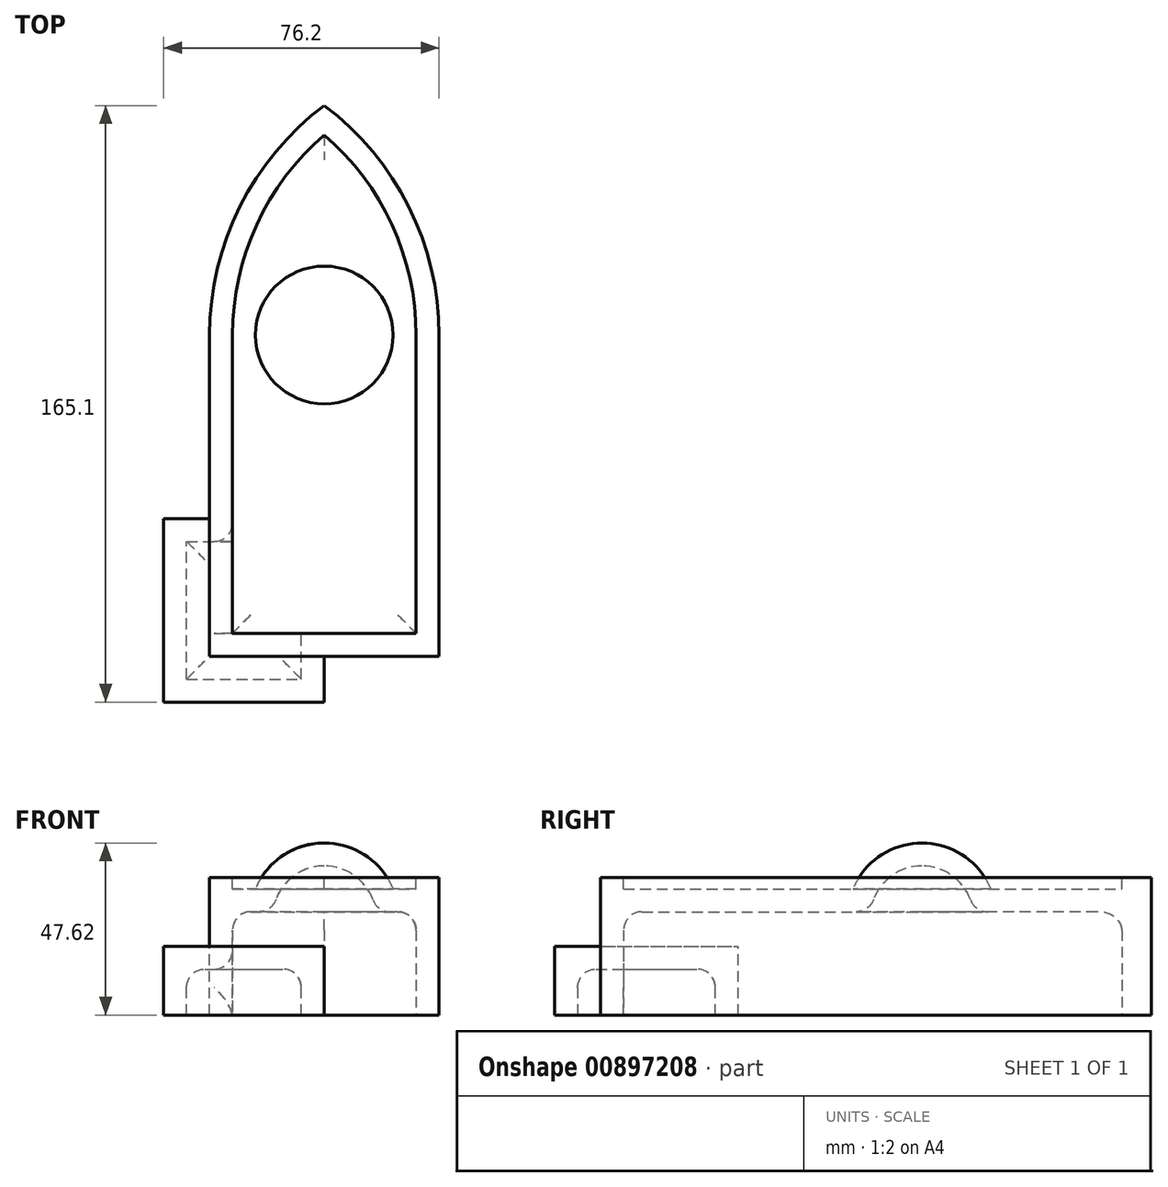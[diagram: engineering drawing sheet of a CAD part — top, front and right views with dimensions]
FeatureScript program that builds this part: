
annotation { "Feature Type Name" : "Feature", "Feature Type Description" : "" }
export const myFeature = defineFeature(function(context is Context, id is Id, definition is map)
    precondition{}
    {
        {
            var Q0;
            Q0=qCreatedBy(makeId("Top.planeOp"),FACE);
            var sketch = newSketch(context, id + "F0", { "sketchPlane" : qUnion([Q0])});
            skLineSegment(sketch, "E0.bottom", {"start": v(0, 0) * mm, "end": v(63.5, 0) * mm});
            skLineSegment(sketch, "E0.top", {"start": v(0, 88.9) * mm, "end": v(63.5, 88.9) * mm, "construction": true});
            skLineSegment(sketch, "E0.left", {"start": v(0, 0) * mm, "end": v(0, 88.9) * mm});
            skLineSegment(sketch, "E0.right", {"start": v(63.5, 0) * mm, "end": v(63.5, 88.9) * mm});
            skLineSegment(sketch, "E1", {"start": v(31.75, 0) * mm, "end": v(31.75, 152.4) * mm, "construction": true});
            skArc(sketch, "E2", {"start": v(31.75, 152.4) * mm, "mid": v(8.38, 124.4) * mm, "end": v(0, 88.9) * mm});
            skArc(sketch, "E3.MirrorCS", {"start": v(31.75, 152.4) * mm, "mid": v(55.12, 124.4) * mm, "end": v(63.5, 88.9) * mm});
            skSolve(sketch);
        }
        {
            var Q0;
            Q0 = qSketchRegion(id + "F0", true);
            extrude(context, id + "F1", {"entities" : qUnion([Q0]), "depth" : 38.1 * mm, "offsetDistance" : 25.4 * mm});
        }
        {
            var Q0;
            Q0=makeQuery(id+"F1.opExtrude","SWEPT_FACE",FACE,{"disambiguationData":[OSD([sQuery(id+"F0.wireOp",EDGE,"E0.left")])]});
            var sketch = newSketch(context, id + "F2", { "sketchPlane" : qUnion([Q0])});
            skLineSegment(sketch, "E4.bottom", {"start": v(0, 0) * mm, "end": v(-38.1, 0) * mm});
            skLineSegment(sketch, "E4.top", {"start": v(0, 19.05) * mm, "end": v(-38.1, 19.05) * mm});
            skLineSegment(sketch, "E4.left", {"start": v(0, 0) * mm, "end": v(0, 19.05) * mm});
            skLineSegment(sketch, "E4.right", {"start": v(-38.1, 0) * mm, "end": v(-38.1, 19.05) * mm});
            skSolve(sketch);
        }
        {
            var Q0;
            Q0 = qSketchRegion(id + "F2", true);
            extrude(context, id + "F3", {"entities" : qUnion([Q0]), "operationType" : NewBodyOperationType.ADD, "depth" : 12.7 * mm, "offsetDistance" : 25.4 * mm});
        }
        {
            var Q0;
            Q0=makeQuery(id+"F3.boolean.opBoolean","MERGE",FACE,{"derivedFrom":[makeQuery(id+"F1.opExtrude","SWEPT_FACE",FACE,{"disambiguationData":[OSD([sQuery(id+"F0.wireOp",EDGE,"E0.bottom")])]}),makeQuery(id+"F3.opExtrude","SWEPT_FACE",FACE,{"disambiguationData":[OSD([sQuery(id+"F2.wireOp",EDGE,"E4.left")])]})]});
            var sketch = newSketch(context, id + "F4", { "sketchPlane" : qUnion([Q0])});
            skLineSegment(sketch, "E5.bottom", {"start": v(-12.7, 0) * mm, "end": v(31.75, 0) * mm});
            skLineSegment(sketch, "E5.top", {"start": v(-12.7, 19.05) * mm, "end": v(31.75, 19.05) * mm});
            skLineSegment(sketch, "E5.left", {"start": v(-12.7, 0) * mm, "end": v(-12.7, 19.05) * mm});
            skLineSegment(sketch, "E5.right", {"start": v(31.75, 0) * mm, "end": v(31.75, 19.05) * mm});
            skSolve(sketch);
        }
        {
            var Q0;
            Q0 = qSketchRegion(id + "F4", true);
            extrude(context, id + "F5", {"entities" : qUnion([Q0]), "operationType" : NewBodyOperationType.ADD, "depth" : 12.7 * mm, "offsetDistance" : 25.4 * mm});
        }
        {
            var Q0;
            Q0=makeQuery(id+"F1.opExtrude","CAP_FACE",FACE,{"disambiguationData":[OSD([sQuery(id+"F0.wireOp",EDGE,"E0.bottom"),sQuery(id+"F0.wireOp",EDGE,"E0.left"),sQuery(id+"F0.wireOp",EDGE,"E0.right"),sQuery(id+"F0.wireOp",EDGE,"E2"),sQuery(id+"F0.wireOp",EDGE,"E3.MirrorCS")])],"isStart":false});
            var sketch = newSketch(context, id + "F6", { "sketchPlane" : qUnion([Q0])});
            skLineSegment(sketch, "E6.0", {"start": v(6.35, 6.35) * mm, "end": v(6.35, 88.9) * mm});
            skArc(sketch, "E6.1", {"start": v(31.75, 144.26) * mm, "mid": v(13, 119.35) * mm, "end": v(6.35, 88.9) * mm});
            skLineSegment(sketch, "E6.2", {"start": v(6.35, 6.35) * mm, "end": v(57.15, 6.35) * mm});
            skLineSegment(sketch, "E6.3", {"start": v(57.15, 6.35) * mm, "end": v(57.15, 88.9) * mm});
            skArc(sketch, "E6.4", {"start": v(31.75, 144.26) * mm, "mid": v(50.5, 119.35) * mm, "end": v(57.15, 88.9) * mm});
            skSolve(sketch);
        }
        {
            var Q0;
            Q0 = qSketchRegion(id + "F6", true);
            extrude(context, id + "F7", {"entities" : qUnion([Q0]), "operationType" : NewBodyOperationType.REMOVE, "oppositeDirection" : true, "depth" : 3.17 * mm, "offsetDistance" : 25.4 * mm});
        }
        {
            var Q0;
            Q0=makeQuery(id+"F1.opExtrude","SWEPT_EDGE",EDGE,{"disambiguationData":[OSD([sQuery(id+"F0.wireOp",EDGE,"E0.left"),sQuery(id+"F0.wireOp",EDGE,"E2")])]});
            cPoint(context, id + "F8", {"entities" : qUnion([Q0]), "parameter" : 0.5});
        }
        {
            var Q0;
            Q0=qCreatedBy(makeId("Front.planeOp"),FACE);
            var Q1;
            Q1 = qCreatedBy(id + "F8" ,VERTEX);
            cPlane(context, id + "F9", {"entities" : qUnion([Q0, Q1]), "cplaneType" : CPlaneType.PLANE_POINT, "offset" : 0 * mm, "width" : 152.4 * mm, "height" : 152.4 * mm});
        }
        {
            var Q0;
            Q0=qCreatedBy(id+"F9.planeOp",FACE);
            var sketch = newSketch(context, id + "F10", { "sketchPlane" : qUnion([Q0])});
            skLineSegment(sketch, "E7.0", {"start": v(0, 38.1) * mm, "end": v(63.5, 38.1) * mm, "construction": true});
            skLineSegment(sketch, "E8", {"start": v(31.75, 38.1) * mm, "end": v(31.75, 80.25) * mm, "construction": true});
            skLineSegment(sketch, "E9", {"start": v(6.64, 34.93) * mm, "end": v(55.04, 34.93) * mm, "construction": true});
            skArc(sketch, "E10", {"start": v(31.75, 47.63) * mm, "mid": v(20.3, 44.16) * mm, "end": v(12.7, 34.92) * mm});
            skLineSegment(sketch, "E11", {"start": v(31.75, 47.63) * mm, "end": v(31.75, 34.93) * mm});
            skPoint(sketch, "E11.endSnap0", {"position": v(30.84, 34.93) * mm});
            skLineSegment(sketch, "E12", {"start": v(31.75, 34.93) * mm, "end": v(12.7, 34.92) * mm});
            skSolve(sketch);
        }
        {
            var Q0;
            Q0 = qSketchRegion(id + "F10", true);
            var Q1;
            Q1=sQuery(id+"F10.wireOp",EDGE,"E8");
            revolve(context, id + "F11", {"operationType" : NewBodyOperationType.ADD, "surfaceOperationType" : NewSurfaceOperationType.NEW, "entities" : qUnion([Q0]), "axis" : qUnion([Q1]), "revolveType" : RevolveType.FULL});
        }
        {
            var Q0;
            Q0=makeQuery(id+"F5.boolean.opBoolean","MERGE",FACE,{"derivedFrom":[makeQuery(id+"F3.boolean.opBoolean","MERGE",FACE,{"derivedFrom":[makeQuery(id+"F1.opExtrude","CAP_FACE",FACE,{"disambiguationData":[OSD([sQuery(id+"F0.wireOp",EDGE,"E0.bottom"),sQuery(id+"F0.wireOp",EDGE,"E0.left"),sQuery(id+"F0.wireOp",EDGE,"E0.right"),sQuery(id+"F0.wireOp",EDGE,"E2"),sQuery(id+"F0.wireOp",EDGE,"E3.MirrorCS")])],"isStart":true}),makeQuery(id+"F3.opExtrude","SWEPT_FACE",FACE,{"disambiguationData":[OSD([sQuery(id+"F2.wireOp",EDGE,"E4.bottom")])]})]}),makeQuery(id+"F5.opExtrude","SWEPT_FACE",FACE,{"disambiguationData":[OSD([sQuery(id+"F4.wireOp",EDGE,"E5.bottom")])]})]});
            shell(context, id + "F12", {"entities" : qUnion([Q0]), "thickness" : 6.35 * mm});
        }
        {
            var Q0;
            Q0=makeQuery(id+"F12.opShell","TWEAK_EDGE",EDGE,{"derivedFrom":[makeQuery(id+"F1.opExtrude","SWEPT_FACE",FACE,{"disambiguationData":[OSD([sQuery(id+"F0.wireOp",EDGE,"E0.left")])]}),makeQuery(id+"F7.boolean.opBoolean","COPY",FACE,{"derivedFrom":makeQuery(id+"F7.opExtrude","CAP_FACE",FACE,{"disambiguationData":[OSD([sQuery(id+"F6.wireOp",EDGE,"E6.0"),sQuery(id+"F6.wireOp",EDGE,"E6.1"),sQuery(id+"F6.wireOp",EDGE,"E6.2"),sQuery(id+"F6.wireOp",EDGE,"E6.3"),sQuery(id+"F6.wireOp",EDGE,"E6.4")])],"isStart":false})})]});
            var Q1;
            Q1=makeQuery(id+"F12.opShell","TWEAK_EDGE",EDGE,{"derivedFrom":[makeQuery(id+"F1.opExtrude","SWEPT_FACE",FACE,{"disambiguationData":[OSD([sQuery(id+"F0.wireOp",EDGE,"E3.MirrorCS")])]}),makeQuery(id+"F7.boolean.opBoolean","COPY",FACE,{"derivedFrom":makeQuery(id+"F7.opExtrude","CAP_FACE",FACE,{"disambiguationData":[OSD([sQuery(id+"F6.wireOp",EDGE,"E6.0"),sQuery(id+"F6.wireOp",EDGE,"E6.1"),sQuery(id+"F6.wireOp",EDGE,"E6.2"),sQuery(id+"F6.wireOp",EDGE,"E6.3"),sQuery(id+"F6.wireOp",EDGE,"E6.4")])],"isStart":false})})]});
            var Q2;
            Q2=makeQuery(id+"F12.opShell","TWEAK_EDGE",EDGE,{"derivedFrom":[makeQuery(id+"F3.boolean.opBoolean","MERGE",FACE,{"derivedFrom":[makeQuery(id+"F1.opExtrude","SWEPT_FACE",FACE,{"disambiguationData":[OSD([sQuery(id+"F0.wireOp",EDGE,"E0.bottom")])]}),makeQuery(id+"F3.opExtrude","SWEPT_FACE",FACE,{"disambiguationData":[OSD([sQuery(id+"F2.wireOp",EDGE,"E4.left")])]})]}),makeQuery(id+"F7.boolean.opBoolean","COPY",FACE,{"derivedFrom":makeQuery(id+"F7.opExtrude","CAP_FACE",FACE,{"disambiguationData":[OSD([sQuery(id+"F6.wireOp",EDGE,"E6.0"),sQuery(id+"F6.wireOp",EDGE,"E6.1"),sQuery(id+"F6.wireOp",EDGE,"E6.2"),sQuery(id+"F6.wireOp",EDGE,"E6.3"),sQuery(id+"F6.wireOp",EDGE,"E6.4")])],"isStart":false})})]});
            var Q3;
            Q3=makeQuery(id+"F12.opShell","OFFSET_EDGE",EDGE,{"disambiguationData":[OSD([sQuery(id+"F2.wireOp",EDGE,"E4.top")])]});
            var Q4;
            {var subQ0=sQuery(id+"F4.wireOp",EDGE,"E5.top");Q4=makeQuery(id+"F12.opShell","OFFSET_EDGE",EDGE,{"disambiguationData":[OSD([subQ0]),TDD([makeQuery(id+"F5.opExtrude","CAP_EDGE",EDGE,{"disambiguationData":[OSD([subQ0])],"isStart":true})])]});}
            var Q5;
            {var subQ0=sQuery(id+"F4.wireOp",EDGE,"E5.top");Q5=makeQuery(id+"F12.opShell","OFFSET_EDGE",EDGE,{"disambiguationData":[OSD([subQ0]),TDD([makeQuery(id+"F5.opExtrude","CAP_EDGE",EDGE,{"disambiguationData":[OSD([subQ0])],"isStart":false})])]});}
            var Q6;
            Q6=makeQuery(id+"F12.opShell","OFFSET_EDGE",EDGE,{"disambiguationData":[OSD([sQuery(id+"F2.wireOp",EDGE,"E4.top"),sQuery(id+"F4.wireOp",EDGE,"E5.top"),sQuery(id+"F4.wireOp",EDGE,"E5.left")])]});
            var Q7;
            Q7=makeQuery(id+"F12.opShell","OFFSET_EDGE",EDGE,{"disambiguationData":[OSD([sQuery(id+"F2.wireOp",EDGE,"E4.top"),sQuery(id+"F2.wireOp",EDGE,"E4.right")])]});
            var Q8;
            Q8=makeQuery(id+"F12.opShell","OFFSET_EDGE",EDGE,{"disambiguationData":[OSD([sQuery(id+"F4.wireOp",EDGE,"E5.top"),sQuery(id+"F4.wireOp",EDGE,"E5.right")])]});
            var Q9;
            Q9=makeQuery(id+"F12.opShell","OFFSET_EDGE",EDGE,{"disambiguationData":[OSD([sQuery(id+"F10.wireOp",EDGE,"E10"),sQuery(id+"F10.wireOp",EDGE,"E12")])]});
            fillet(context, id + "F13", {"entities" : qUnion([Q0, Q1, Q2, Q3, Q4, Q5, Q6, Q7, Q8, Q9]), "radius" : 5.08 * mm, "tangentPropagation" : true, "allowEdgeOverflow" : false});
        }
    });
